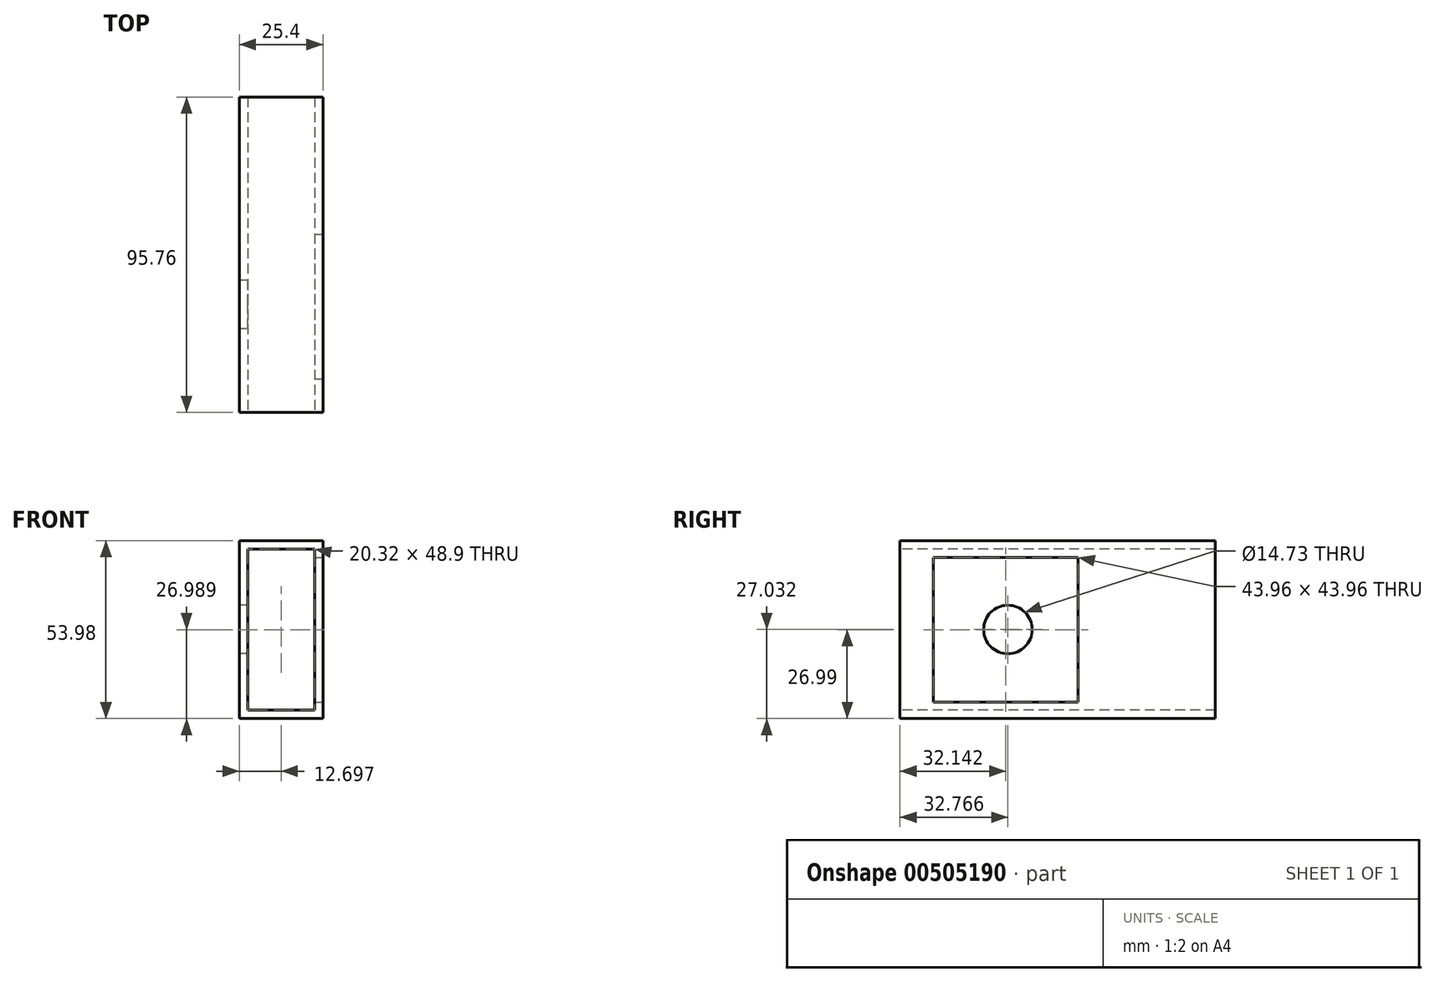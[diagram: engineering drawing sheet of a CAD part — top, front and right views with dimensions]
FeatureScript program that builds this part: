
annotation { "Feature Type Name" : "Feature", "Feature Type Description" : "" }
export const myFeature = defineFeature(function(context is Context, id is Id, definition is map)
    precondition{}
    {
        {
            var Q0;
            Q0=qCreatedBy(makeId("Front.planeOp"),FACE);
            var sketch = newSketch(context, id + "F0", { "sketchPlane" : qUnion([Q0])});
            skLineSegment(sketch, "E0.bottom", {"start": v(-69.82, -19.36) * mm, "end": v(-44.42, -19.36) * mm});
            skLineSegment(sketch, "E0.top", {"start": v(-69.82, -73.34) * mm, "end": v(-44.42, -73.34) * mm});
            skLineSegment(sketch, "E0.left", {"start": v(-69.82, -19.36) * mm, "end": v(-69.82, -73.34) * mm});
            skLineSegment(sketch, "E0.right", {"start": v(-44.42, -19.36) * mm, "end": v(-44.42, -73.34) * mm});
            skLineSegment(sketch, "E1.0", {"start": v(-67.28, -21.9) * mm, "end": v(-67.28, -70.8) * mm});
            skLineSegment(sketch, "E1.1", {"start": v(-67.28, -21.9) * mm, "end": v(-46.96, -21.9) * mm});
            skLineSegment(sketch, "E1.2", {"start": v(-46.96, -21.9) * mm, "end": v(-46.96, -70.8) * mm});
            skLineSegment(sketch, "E1.3", {"start": v(-67.28, -70.8) * mm, "end": v(-46.96, -70.8) * mm});
            skSolve(sketch);
        }
        {
            var Q0;
            Q0=qSketchRegion(id+"F0",true);
            extrude(context, id + "F1", {"entities" : qUnion([Q0]), "oppositeDirection" : true, "depth" : 95.76 * mm});
        }
        {
            var Q0;
            Q0=makeQuery(id+"F1.opExtrude","SWEPT_FACE",FACE,{"disambiguationData":[OSD([sQuery(id+"F0.wireOp",EDGE,"E0.left")])]});
            var sketch = newSketch(context, id + "F2", { "sketchPlane" : qUnion([Q0])});
            skPoint(sketch, "E2", {"position": v(-32.77, -46.3) * mm});
            skPoint(sketch, "E2.positionSnap0", {"position": v(-32.77, -20.9) * mm});
            skPoint(sketch, "E2.positionSnap1", {"position": v(-106.36, -46.3) * mm});
            skCircle(sketch, "E3", {"center": v(-32.77, -46.3) * mm, "radius": 7.37 * mm});
            skSolve(sketch);
        }
        {
            var Q0;
            Q0=makeQuery(id+"F2.imprint","IMPRINT",FACE,{"disambiguationData":[TD([[makeQuery(id+"F2.imprint","IMPRINT",EDGE,{"derivedFrom":sQuery(id+"F2.wireOp",EDGE,"E3")}),1.0]])]});
            extrude(context, id + "F3", {"entities" : qUnion([Q0]), "operationType" : NewBodyOperationType.REMOVE, "oppositeDirection" : true, "depth" : 50.3 * mm});
        }
        {
            var Q0;
            Q0=makeQuery(id+"F1.opExtrude","SWEPT_FACE",FACE,{"disambiguationData":[OSD([sQuery(id+"F0.wireOp",EDGE,"E0.right")])]});
            var sketch = newSketch(context, id + "F4", { "sketchPlane" : qUnion([Q0])});
            skLineSegment(sketch, "E4.bottom", {"start": v(10.16, -24.37) * mm, "end": v(54.12, -24.37) * mm});
            skLineSegment(sketch, "E4.top", {"start": v(10.16, -68.33) * mm, "end": v(54.12, -68.33) * mm});
            skLineSegment(sketch, "E4.left", {"start": v(10.16, -24.37) * mm, "end": v(10.16, -68.33) * mm});
            skLineSegment(sketch, "E4.right", {"start": v(54.12, -24.37) * mm, "end": v(54.12, -68.33) * mm});
            skPoint(sketch, "E5.endSnap0", {"position": v(0, -46.35) * mm});
            skSolve(sketch);
        }
        {
            var Q0;
            Q0=makeQuery(id+"F4.imprint","IMPRINT",FACE,{"disambiguationData":[TD([[makeQuery(id+"F4.imprint","IMPRINT",EDGE,{"derivedFrom":sQuery(id+"F4.wireOp",EDGE,"E4.bottom")}),-1.0]])]});
            extrude(context, id + "F5", {"entities" : qUnion([Q0]), "operationType" : NewBodyOperationType.REMOVE, "oppositeDirection" : true, "depth" : 9.9 * mm});
        }
    });
